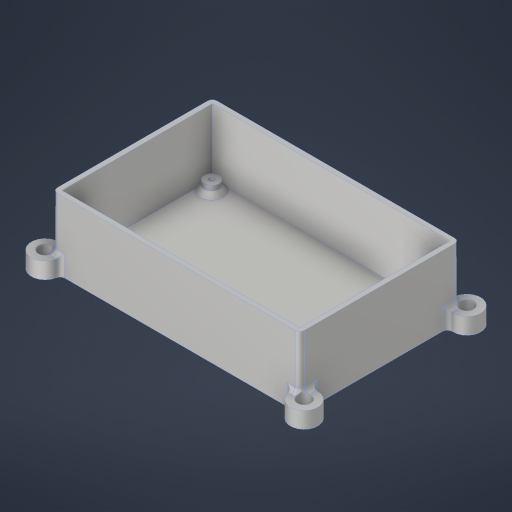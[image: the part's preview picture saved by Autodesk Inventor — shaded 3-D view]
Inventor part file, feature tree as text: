
AUTODESK INVENTOR PART (.ipt)
format: ipt  version: 2023 (Build 270158000, 158)  size: 362,496 bytes
history: native  units: in
note: dims shown in document units (in); Inventor stores cm internally (conversion verified against a paired STEP export)
features: sketch x3, extrude x3, fillet x2, projected_geometry x2, shell x1, hole x1, chamfer x1
ambient origin geometry x8: Origin, YZ Plane, XZ Plane, XY Plane, X Axis, Y Axis, Z Axis, Center Point
bodies: Solid1 (feature_tree)
feature tree (13):
  sketch  "Sketch1"  dims[d0=2.2004in d1=3.6951in d2=4.0157in d3=2.5394in]
  extrude  "Extrusion1"  Depth=3.6951in
  fillet  "Fillet1"  Radius=4.0157in
  shell  "Shell1"  Thickness=2.5394in
  hole  "Hole1"  [1 undecoded]
  extrude  "Extrusion2"  Depth=0.0787in
  chamfer  "Chamfer1"  Distance=0.0787in
  extrude  "Extrusion3"  Depth=0.0787in
  fillet  "Fillet2"  Radius=0.1575in
  sketch  "Sketch2"  dims[d4=0.0787in d5=0.0787in]
  projected_geometry  "Projected Loop1"
  sketch  "Sketch3"  dims[d6=1.1811in d7=0.0in d8=0.0787in d9=0.0787in d10=0.0968in d11=0.2362in d12=1.125in d13=0.0787in d14=0.5635in d15=0.315in d16=0.8108in d17=0.0787in d18=0.1575in d19=0.0in d20=0.0787in d21=0.0787in d22=45.0deg d23=4.375in d24=2.75in d25=0.2283in d26=0.1181in d27=0.2756in d28=0.0in d29=0.0787in]
  projected_geometry  "Projected Loop2"
note: 1 required parameter value undecoded (feature->parameter linkage not recoverable at this tier; creation-order binding heuristic only, values carry confidence <= 0.55)
